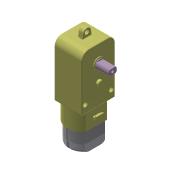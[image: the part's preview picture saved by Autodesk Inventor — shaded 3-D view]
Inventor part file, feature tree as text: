
AUTODESK INVENTOR PART (.ipt)
format: ipt  version: 2016 (Build 200138000, 138)  size: 567,808 bytes
history: native  units: mm
features: sketch x19, extrude x18, fillet x5, plane x4, move_body x4, mirror x3, loft x1, chamfer x1, split x1, projected_geometry x1
ambient origin geometry x8: Origin, YZ Plane, XZ Plane, XY Plane, X Axis, Y Axis, Z Axis, Center Point
bodies: Solid1 (feature_tree)
feature tree (57):
  extrude  "Extrusion1"  Depth=36.5mm
  fillet  "Fillet1"  Radius=18.5mm
  sketch  "Sketch2"  dims[d4=5.0mm d5=3.0mm]
  extrude  "Extrusion4"  Depth=3.0mm
  plane  "Work Plane8"
  loft  "Loft1"
  sketch  "Sketch9"  dims[d19=0.0mm d24=12.0mm d25=0.0mm]
  fillet  "Fillet3"  Radius=8.15mm
  extrude  "Extrusion6"  Depth=22.3mm
  extrude  "Extrusion7"  Depth=12.0mm TaperAngle=0.0deg
  extrude  "Extrusion8"  Depth=3.0mm
  extrude  "Extrusion9"  Depth=0.75mm
  extrude  "Extrusion10"  TaperAngle=0.0deg  [1 undecoded]
  extrude  "Extrusion11"  Depth=2.6mm
  extrude  "Extrusion12"  Depth=2.5mm
  plane  "Work Plane9"
  mirror  "Mirror1"
  extrude  "Extrusion13"  Depth=7.3mm
  chamfer  "Chamfer1"  Distance=0.5mm
  extrude  "Extrusion14"  Depth=0.5mm TaperAngle=0.0deg
  plane  "Work Plane10"
  mirror  "Mirror2"
  extrude  "Extrusion16"  Depth=0.9mm
  plane  "Work Plane13"
  split  "Split2"
  extrude  "Extrusion17"  Depth=1.9mm
  extrude  "Extrusion18"  Depth=0.9mm
  mirror  "Mirror4"
  extrude  "Extrusion19"  Depth=10.0mm
  extrude  "Extrusion20"  Depth=10.0mm
  extrude  "Extrusion22"  Depth=10.0mm
  extrude  "Extrusion23"  Depth=10.0mm
  fillet  "Fillet6"  Radius=1.75mm
  fillet  "Fillet7"  Radius=3.0mm
  fillet  "Fillet8"  Radius=1.0mm
  move_body  "Move Body1"
  move_body  "Move Body2"
  move_body  "Move Body3"
  move_body  "Move Body4"
  sketch  "Sketch1"  dims[d0=22.5mm d1=36.5mm d2=18.5mm d3=0.0mm]
  sketch  "Sketch5"  dims[d6=6.0mm d7=7.75mm d8=8.15mm]
  sketch  "Sketch8"  dims[d17=17.0mm d18=22.3mm]
  sketch  "Sketch10"  dims[d33=5.5mm d34=3.0mm]
  sketch  "Sketch11"  dims[d35=4.5mm d36=0.75mm]
  sketch  "Sketch12"  dims[d37=0.0mm d38=0.0mm d39=90.0deg]
  sketch  "Sketch13"  dims[d40=0.0mm d41=90.0deg d42=2.6mm]
  sketch  "Sketch14"  dims[d43=3.0mm d45=2.5mm]
  sketch  "Sketch15"  dims[d46=3.0mm d47=0.0mm d48=7.3mm]
  sketch  "Sketch16"  dims[d49=11.25mm]
  sketch  "Sketch17"  dims[d50=11.25mm]
  projected_geometry  "Projected Loop1"
  sketch  "Sketch21"  dims[d51=11.25mm d52=0.5mm d53=0.0mm]
  sketch  "Sketch22"  dims[d54=5.5mm d55=0.5mm d56=0.0mm]
  sketch  "Sketch23"  dims[d62=0.9mm d63=0.9mm]
  sketch  "Sketch24"  dims[d66=8.6mm d67=0.0mm d68=1.9mm]
  sketch  "Sketch25"  dims[d69=0.9mm d70=0.9mm]
  sketch  "Sketch26"  dims[d71=9.1mm d72=0.0mm d73=3.7mm d74=5.7mm d75=9.4mm d76=9.4mm d77=1.75mm d78=0.0mm d79=3.0mm d80=1.0mm d81=4.0mm d82=18.5mm d83=0.0mm d84=11.25mm d85=3.5mm d86=5.0mm d89=2.5mm d90=0.0mm d91=2.5mm d92=2.0mm d93=45.0deg d94=1.5mm d95=1.0mm d96=0.0mm d97=8.5mm d102=4.716128mm d103=1.0mm d104=13.3mm d105=0.0mm d106=-5.3mm d107=5.0mm d108=7.5mm d109=3.089042mm d110=1.8mm d111=0.0mm d112=2.5mm d113=5.3mm d114=0.0mm d116=10.0mm d117=3.6mm d118=2.0mm d119=0.0mm d121=2.0mm d122=1.0mm d123=0.0mm d131=2.0mm d132=0.0mm d133=1.0mm d134=2.0mm d135=0.0mm d136=2.0mm d137=0.5mm d138=0.3mm d139=0.0mm d140=10.0mm d141=0.0mm d142=10.0mm d143=0.0mm d144=10.0mm d145=10.0mm d146=0.0mm d147=0.0mm d148=0.0mm d149=0.0mm d150=-100.0mm]
note: 1 required parameter value undecoded (feature->parameter linkage not recoverable at this tier; creation-order binding heuristic only, values carry confidence <= 0.55)
